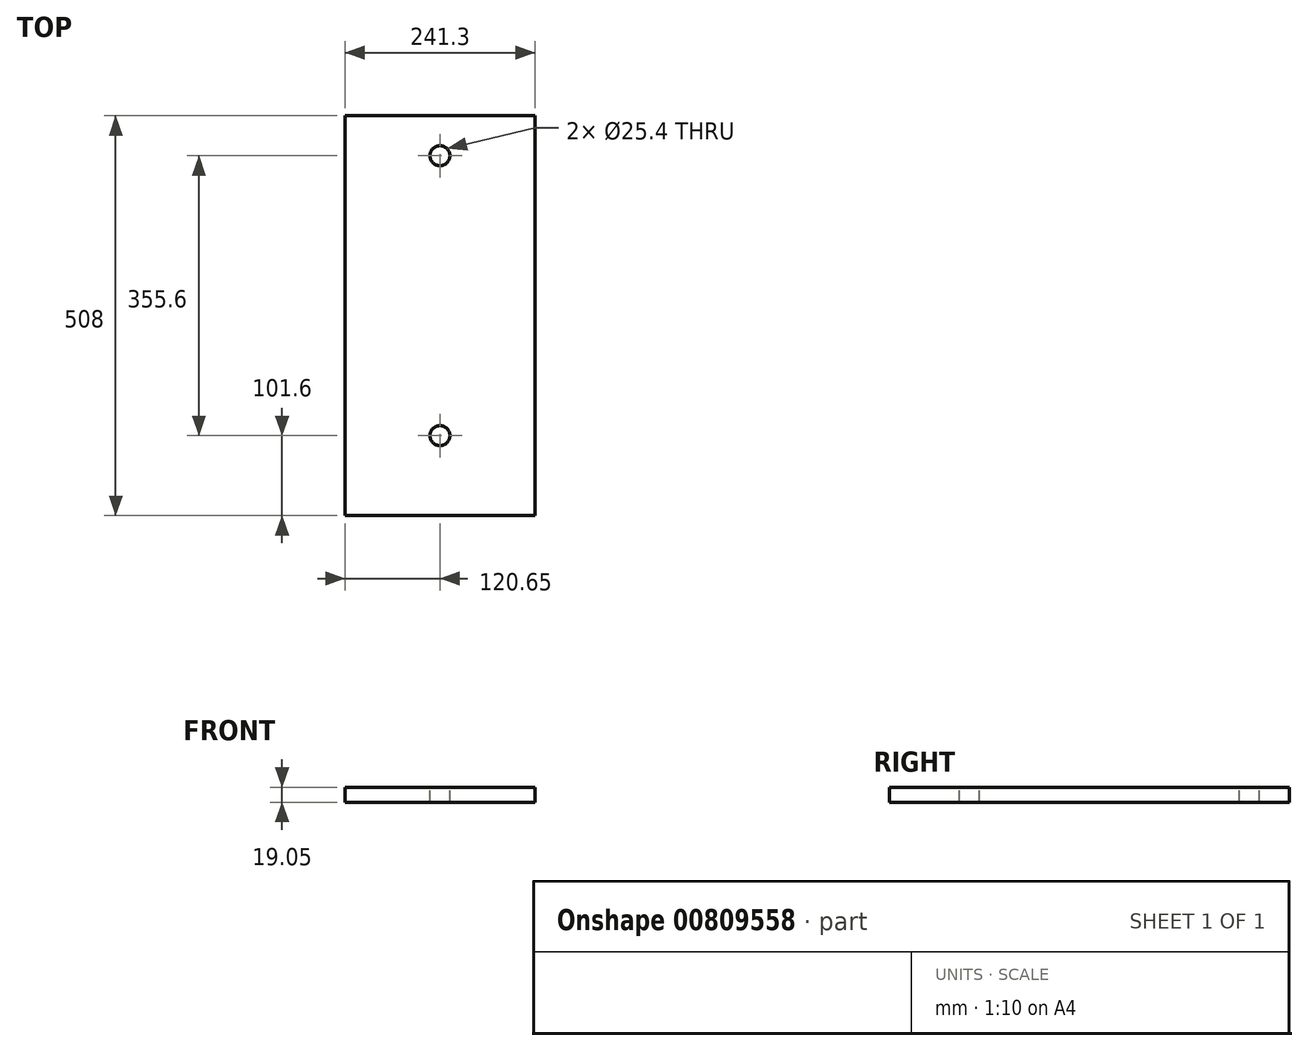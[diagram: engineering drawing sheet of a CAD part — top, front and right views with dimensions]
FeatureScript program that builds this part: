
annotation { "Feature Type Name" : "Feature", "Feature Type Description" : "" }
export const myFeature = defineFeature(function(context is Context, id is Id, definition is map)
    precondition{}
    {
        {
            var Q0;
            Q0=qCreatedBy(makeId("Top.planeOp"),FACE);
            var sketch = newSketch(context, id + "F0", { "sketchPlane" : qUnion([Q0])});
            skLineSegment(sketch, "E0.bottom", {"start": v(120.65, -254) * mm, "end": v(-120.65, -254) * mm});
            skLineSegment(sketch, "E0.top", {"start": v(120.65, 254) * mm, "end": v(-120.65, 254) * mm});
            skLineSegment(sketch, "E0.left", {"start": v(120.65, -254) * mm, "end": v(120.65, 254) * mm});
            skLineSegment(sketch, "E0.right", {"start": v(-120.65, -254) * mm, "end": v(-120.65, 254) * mm});
            skPoint(sketch, "E0.middle", {"position": v(0, 0) * mm});
            skSolve(sketch);
        }
        {
            var Q0;
            Q0=makeQuery(id+"F0.imprint","IMPRINT",FACE,{"disambiguationData":[TD([[makeQuery(id+"F0.imprint","IMPRINT",EDGE,{"derivedFrom":sQuery(id+"F0.wireOp",EDGE,"E0.bottom")}),-1.0]])]});
            extrude(context, id + "F1", {"entities" : qUnion([Q0]), "depth" : 19.05 * mm, "offsetDistance" : 25.4 * mm});
        }
        {
            var Q0;
            Q0=makeQuery(id+"F1.opExtrude","CAP_FACE",FACE,{"disambiguationData":[OSD([sQuery(id+"F0.wireOp",EDGE,"E0.bottom"),sQuery(id+"F0.wireOp",EDGE,"E0.top"),sQuery(id+"F0.wireOp",EDGE,"E0.left"),sQuery(id+"F0.wireOp",EDGE,"E0.right")])],"isStart":false});
            var sketch = newSketch(context, id + "F2", { "sketchPlane" : qUnion([Q0])});
            skLineSegment(sketch, "E1", {"start": v(0, 254) * mm, "end": v(0, 203.2) * mm});
            skCircle(sketch, "E2", {"center": v(0, 203.2) * mm, "radius": 12.7 * mm});
            skLineSegment(sketch, "E3", {"start": v(0, -254) * mm, "end": v(0, -152.4) * mm});
            skCircle(sketch, "E4", {"center": v(0, -152.4) * mm, "radius": 12.7 * mm});
            skSolve(sketch);
        }
        {
            var Q0;
            Q0=makeQuery(id+"F2.imprint","IMPRINT",FACE,{"disambiguationData":[TD([[makeQuery(id+"F2.imprint","IMPRINT",EDGE,{"derivedFrom":sQuery(id+"F2.wireOp",EDGE,"E2")}),1.0]])]});
            var Q1;
            Q1=makeQuery(id+"F2.imprint","IMPRINT",FACE,{"disambiguationData":[TD([[makeQuery(id+"F2.imprint","IMPRINT",EDGE,{"derivedFrom":sQuery(id+"F2.wireOp",EDGE,"E4")}),1.0]])]});
            extrude(context, id + "F3", {"entities" : qUnion([Q0, Q1]), "operationType" : NewBodyOperationType.REMOVE, "endBound" : BoundingType.THROUGH_ALL, "oppositeDirection" : true, "depth" : 25.4 * mm, "offsetDistance" : 25.4 * mm});
        }
    });
